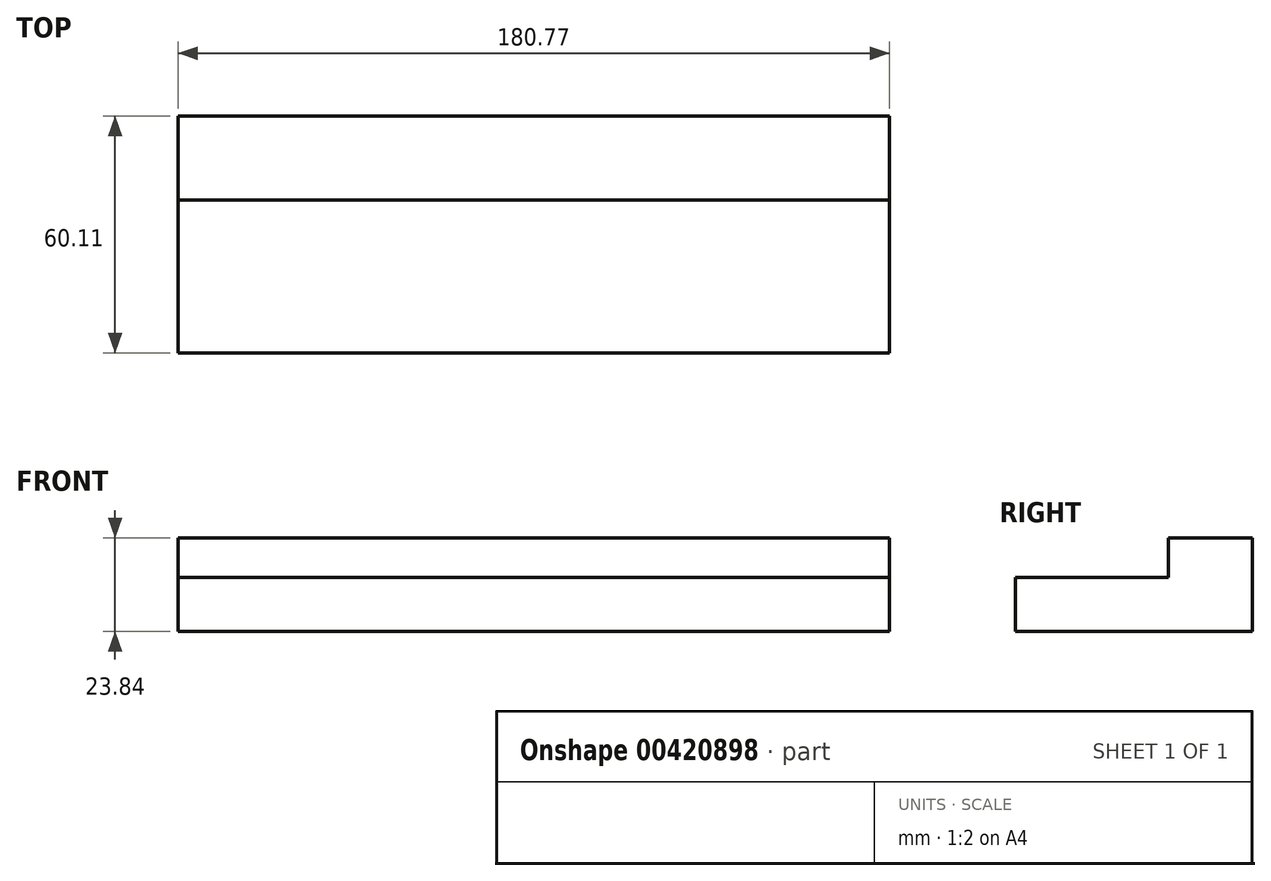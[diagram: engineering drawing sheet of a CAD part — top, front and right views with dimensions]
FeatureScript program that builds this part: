
annotation { "Feature Type Name" : "Feature", "Feature Type Description" : "" }
export const myFeature = defineFeature(function(context is Context, id is Id, definition is map)
    precondition{}
    {
        {
            var Q0;
            Q0=qCreatedBy(makeId("Right.planeOp"),FACE);
            var sketch = newSketch(context, id + "F0", { "sketchPlane" : qUnion([Q0])});
            skLineSegment(sketch, "E0", {"start": v(0, 23.84) * mm, "end": v(-21.31, 23.84) * mm});
            skLineSegment(sketch, "E1", {"start": v(-21.31, 13.82) * mm, "end": v(-60.11, 13.82) * mm});
            skLineSegment(sketch, "E2", {"start": v(-60.11, 13.82) * mm, "end": v(-60.11, 0) * mm});
            skLineSegment(sketch, "E3", {"start": v(-60.11, 0) * mm, "end": v(0, 0) * mm});
            skLineSegment(sketch, "E4", {"start": v(0, 0) * mm, "end": v(0, 23.84) * mm});
            skLineSegment(sketch, "E5", {"start": v(-21.31, 23.84) * mm, "end": v(-21.31, 13.82) * mm});
            skSolve(sketch);
        }
        {
            var Q0;
            Q0=makeQuery(id+"F0.imprint","IMPRINT",FACE,{"disambiguationData":[TD([[makeQuery(id+"F0.imprint","IMPRINT",EDGE,{"derivedFrom":sQuery(id+"F0.wireOp",EDGE,"E0")}),1.0]])]});
            extrude(context, id + "F1", {"entities" : qUnion([Q0]), "depth" : 180.77 * mm});
        }
    });
